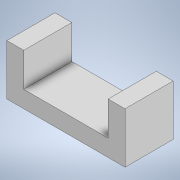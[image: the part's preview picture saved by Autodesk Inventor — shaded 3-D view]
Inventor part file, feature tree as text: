
AUTODESK INVENTOR PART (.ipt)
format: ipt  version: 2021 (Build 250183000, 183)  size: 113,152 bytes
history: native  units: in
note: dims shown in document units (in); Inventor stores cm internally (conversion verified against a paired STEP export)
features: extrude x2, sketch x2
ambient origin geometry x8: Origin, YZ Plane, XZ Plane, XY Plane, X Axis, Y Axis, Z Axis, Center Point
bodies: Solid1 (feature_tree)
feature tree (4):
  extrude  "Extrusion1"  Depth=0.2244in
  extrude  "Extrusion2"  Depth=0.0787in
  sketch  "Sketch1"  dims[d0=0.5512in d1=0.2244in]
  sketch  "Sketch2"  dims[d2=0.0787in d3=0.0in d4=0.0787in d5=0.1575in d6=0.0in]
